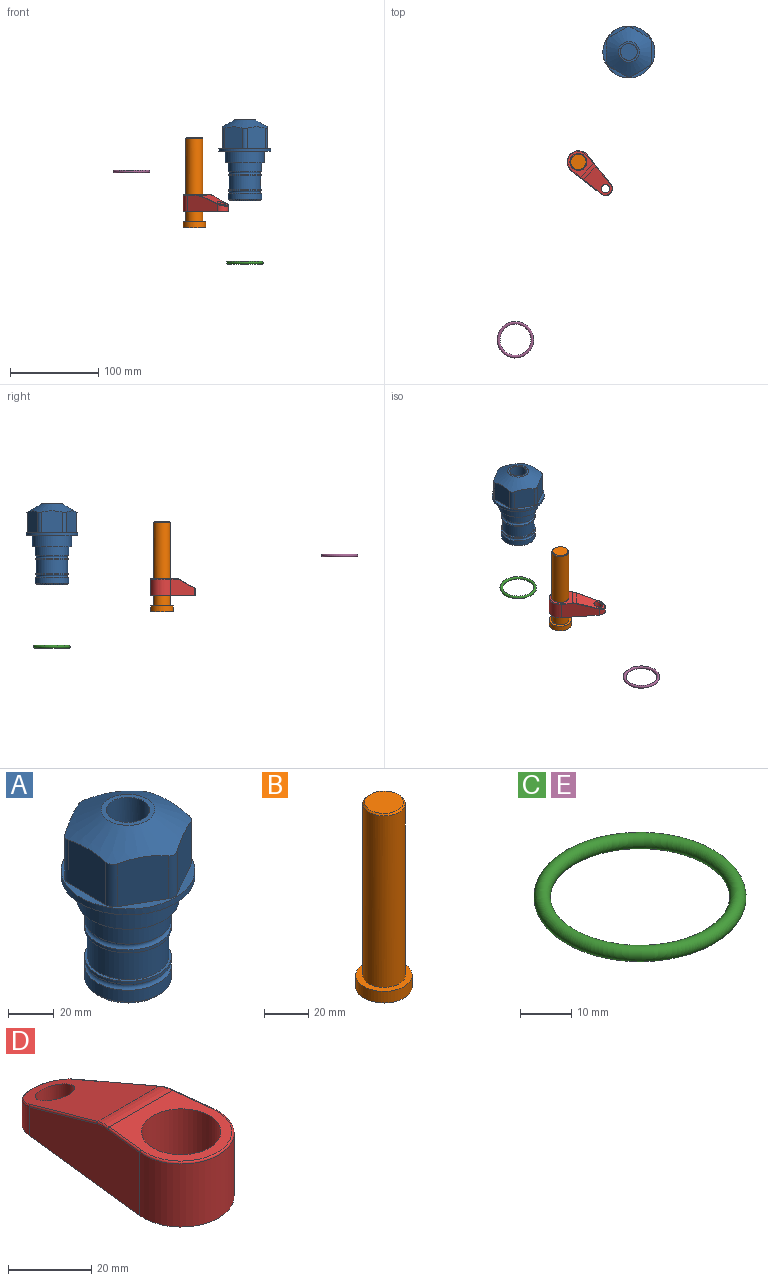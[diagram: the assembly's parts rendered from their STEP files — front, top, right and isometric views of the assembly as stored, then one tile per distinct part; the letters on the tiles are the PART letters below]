
ASSEMBLY  parts=5 mates=2
PART A: 36 faces, bbox 58.7x58.7x91.2 mm
  f0: cylinder r=17.78mm len=35.56mm, axis (0,0,1), area 1670.8mm2, adj f23,f24,f31
  f1: cylinder r=19.05mm len=38.1mm, axis (0,0,1), area 1191.9mm2, adj f26,f27,f30
  f2: plane 58.66x58.66mm, normal (0,0,-1), area 1150.6mm2, adj f3,f28
  f3: cylinder r=29.33mm len=58.66mm, axis (0,0,-1), area 585.1mm2, adj f2,f4
  f4: plane 58.66x58.66mm, normal (0,0,1), area 475.9mm2, adj f3,f5,f6,f7,f8,f9,f10,f11
  f5: plane 24.5x20.32mm, normal (-0.5,0.87,0), area 562.8mm2, adj f4,f15,f16,f17
  f6: plane 24.5x20.32mm, normal (0.5,0.87,0), area 562.8mm2, adj f4,f14,f15,f17
  f7: plane 24.5x23.48mm, normal (1,0,0), area 562.8mm2, adj f4,f13,f14,f17
  f8: plane 24.5x20.32mm, normal (0.5,-0.87,0), area 562.8mm2, adj f4,f12,f13,f17
  f9: plane 24.5x20.32mm, normal (-0.5,-0.87,0), area 562.8mm2, adj f4,f11,f12,f17
  f10: plane 24.5x23.48mm, normal (-1,0,0), area 562.8mm2, adj f4,f11,f16,f17
  f11: cylinder r=5.08mm len=23.01mm, axis (0,0,-1), area 121.2mm2, adj f4,f9,f10,f17
  f12: cylinder r=5.08mm len=23.01mm, axis (0,0,-1), area 121.2mm2, adj f4,f8,f9,f17
  f13: cylinder r=5.08mm len=23.01mm, axis (0,0,-1), area 121.2mm2, adj f4,f7,f8,f17
  f14: cylinder r=5.08mm len=23.01mm, axis (0,0,-1), area 121.2mm2, adj f4,f6,f7,f17
  f15: cylinder r=5.08mm len=23.01mm, axis (0,0,-1), area 121.2mm2, adj f4,f5,f6,f17
  f16: cylinder r=5.08mm len=23.01mm, axis (0,0,-1), area 121.2mm2, adj f4,f5,f10,f17
  f17: cone r=11.73mm half-angle=60deg, axis (0,0,-1), area 2071.8mm2, adj f5,f6,f7,f8,f9,f10,f11,f12
  f18: plane 23.46x23.46mm, normal (0,0,1), area 147.4mm2, adj f17,f35
  f19: plane 34.93x34.93mm, normal (0,0,-1), area 958mm2, adj f29
  f20: cylinder r=19.05mm len=38.1mm, axis (0,0,1), area 760.1mm2, adj f21,f29
  f21: torus R=19.05mm, axis (0,0,1), area 565.3mm2, adj f20,f22
  f22: cylinder r=19.05mm len=38.1mm, axis (0,0,1), area 190mm2, adj f21,f23
  f23: plane 38.1x38.1mm, normal (0,0,1), area 146.9mm2, adj f0,f22
  f24: plane 38.1x38.1mm, normal (0,0,-1), area 146.9mm2, adj f0,f25
  f25: cylinder r=19.05mm len=38.1mm, axis (0,0,1), area 190mm2, adj f24,f26
  f26: torus R=19.05mm, axis (0,0,1), area 565.3mm2, adj f1,f25
  f27: plane 44.45x44.45mm, normal (0,0,-1), area 411.7mm2, adj f1,f28
  f28: cylinder r=22.23mm len=44.45mm, axis (0,0,1), area 1773.5mm2, adj f2,f27
  f29: cone r=19.05mm half-angle=45deg, axis (0,0,1), area 257.5mm2, adj f19,f20
  f30: cylinder r=3.17mm len=6.75mm, axis (-1,0,0), area 128mm2, adj f1,f33
  f31: cylinder r=3.17mm len=6.35mm, axis (-1,0,0), area 102.5mm2, adj f0,f33
  f32: plane 25.4x25.4mm, normal (0,0,1), area 506.7mm2, adj f33
  f33: cylinder r=12.7mm len=66.42mm, axis (0,0,-1), area 5236.2mm2, adj f30,f31,f32,f34
  f34: cone r=9.53mm half-angle=30deg, axis (0,0,-1), area 443.4mm2, adj f33,f35
  f35: cylinder r=9.53mm len=19.05mm, axis (0,0,-1), area 849mm2, adj f18,f34
PART B: 6 faces, bbox 25.4x25.4x101.6 mm
  f0: plane 17.46x17.46mm, normal (0,0,1), area 239.5mm2, adj f5
  f1: plane 25.4x25.4mm, normal (0,0,-1), area 506.7mm2, adj f2
  f2: cylinder r=12.7mm len=25.4mm, axis (0,0,1), area 506.7mm2, adj f1,f3
  f3: plane 25.4x25.4mm, normal (0,0,1), area 221.7mm2, adj f2,f4
  f4: cylinder r=9.53mm len=94.46mm, axis (0,0,1), area 5653mm2, adj f3,f5
  f5: cone r=8.73mm half-angle=45deg, axis (0,0,-1), area 64.4mm2, adj f0,f4
PART C: 1 faces, bbox 44.7x44.7x3.2 mm
  f0: torus R=19.05mm, axis (0,0,1), area 1193.9mm2
PART D: 44 faces, bbox 27.5x64.5x19.1 mm
  f0: plane 2.3x0.95mm, normal (0,0,-1), area 1mm2, adj f25,f30,f34
  f1: plane 63.5x25.4mm, normal (0,0,-1), area 561.7mm2, adj f2,f3,f4,f5,f6,f7,f19,f20
  f2: cylinder r=12.7mm len=25.4mm, axis (0,0,-1), area 792.2mm2, adj f1,f3,f5,f13
  f3: plane 42.33x18.54mm, normal (0.99,0.11,0), area 647mm2, adj f1,f2,f4,f11,f12,f14
  f4: cylinder r=7.94mm len=15.78mm, axis (0,0,-1), area 158.6mm2, adj f1,f3,f5,f16
  f5: plane 42.33x18.54mm, normal (-0.99,0.11,0), area 647mm2, adj f1,f2,f4,f15,f17,f18
  f6: cylinder r=9.53mm len=19.05mm, axis (0,0,-1), area 1140.1mm2, adj f1,f8
  f7: cylinder r=4.76mm len=10.98mm, axis (0,0,-1), area 276.1mm2, adj f1,f9
  f8: plane 25.83x24.38mm, normal (0,0,1), area 262.2mm2, adj f6,f10,f11,f13,f15
  f9: plane 32.49x20.55mm, normal (0,0.34,0.94), area 489.9mm2, adj f7,f10,f14,f16,f18
  f10: cylinder r=12.7mm len=21.49mm, axis (-1,0,0), area 93.2mm2, adj f8,f9,f12,f17
  f11: cylinder r=0.51mm len=12.34mm, axis (0.11,-0.99,0), area 9.9mm2, adj f3,f8,f12,f13
  f12: bspline ~7.62x1.64mm, area 3.5mm2, adj f3,f10,f11,f14
  f13: torus R=12.19mm, axis (0,0,1), area 33.6mm2, adj f2,f8,f11,f15
  f14: cylinder r=0.51mm len=26.01mm, axis (0.1,-0.93,0.34), area 21.6mm2, adj f3,f9,f12,f16
  f15: cylinder r=0.51mm len=12.34mm, axis (0.11,0.99,0), area 9.9mm2, adj f5,f8,f13,f17
  f16: bspline ~15.78x7.05mm, area 15.7mm2, adj f4,f9,f14,f18
  f17: bspline ~7.62x1.64mm, area 3.5mm2, adj f5,f10,f15,f18
  f18: cylinder r=0.51mm len=26.01mm, axis (0.1,0.93,-0.34), area 21.6mm2, adj f5,f9,f16,f17
  f19: plane 21.6x14.29mm, normal (-0.99,-0.11,0), area 242.6mm2, adj f1,f26,f28,f34,f36,f38
  f20: plane 21.6x14.29mm, normal (0.99,-0.11,0), area 242.6mm2, adj f1,f27,f29,f37,f39,f41
  f21: cylinder r=12.7mm len=14.29mm, axis (0,0,-1), area 173.2mm2, adj f1,f26,f27,f30,f31,f33
  f22: cylinder r=7.94mm len=7.63mm, axis (0,0,-1), area 53.8mm2, adj f1,f28,f29,f42
  f23: plane 2.3x0.95mm, normal (0,0,-1), area 1mm2, adj f25,f33,f37
  f24: plane 17.94x12.32mm, normal (0,-0.34,-0.94), area 191.2mm2, adj f25,f38,f41,f42
  f25: cylinder r=9.53mm len=12.93mm, axis (-1,0,0), area 37.5mm2, adj f0,f23,f24,f31,f36,f39
  f26: cylinder r=1.59mm len=14.29mm, axis (0,0,-1), area 49mm2, adj f1,f19,f21,f32
  f27: cylinder r=1.59mm len=14.29mm, axis (0,0,-1), area 49mm2, adj f1,f20,f21,f35
  f28: cylinder r=1.59mm len=7.28mm, axis (0,0,-1), area 22.1mm2, adj f1,f19,f22,f40
  f29: cylinder r=1.59mm len=7.28mm, axis (0,0,-1), area 22.1mm2, adj f1,f20,f22,f43
  f30: torus R=14.29mm, axis (0,0,1), area 5.8mm2, adj f0,f21,f31,f32
  f31: bspline ~11.06x2.73mm, area 20.8mm2, adj f21,f25,f30,f33
  f32: sphere r=1.59mm, area 5.4mm2, adj f26,f30,f34
  f33: torus R=14.29mm, axis (0,0,1), area 5.8mm2, adj f21,f23,f31,f35
  f34: cylinder r=1.59mm len=1.68mm, axis (-0.11,0.99,0), area 2.4mm2, adj f0,f19,f32,f36
  f35: sphere r=1.59mm, area 5.4mm2, adj f27,f33,f37
  f36: bspline ~5.82x2.33mm, area 7.7mm2, adj f19,f25,f34,f38
  f37: cylinder r=1.59mm len=1.68mm, axis (0.11,0.99,0), area 2.4mm2, adj f20,f23,f35,f39
  f38: cylinder r=1.59mm len=18.33mm, axis (0.1,-0.93,0.34), area 46.7mm2, adj f19,f24,f36,f40
  f39: bspline ~5.82x2.33mm, area 7.7mm2, adj f20,f25,f37,f41
  f40: sphere r=1.59mm, area 3.6mm2, adj f28,f38,f42
  f41: cylinder r=1.59mm len=18.33mm, axis (0.1,0.93,-0.34), area 46.7mm2, adj f20,f24,f39,f43
  f42: bspline ~8.31x1.84mm, area 15.3mm2, adj f22,f24,f40,f43
  f43: sphere r=1.59mm, area 3.6mm2, adj f29,f41,f42
PART E: same geometry as C
PLACE A t=(128.27,325.41,-1.63)mm
PLACE B t=(71.22,201.06,-59.88)mm fixed
PLACE C t=(128.27,325.41,-103.07)mm
PLACE D rot(axis=(0,0,-1),134.5deg) t=(71.22,201.06,-69.58)mm
PLACE E at identity
MATE cylindrical C.f0 <-> A.f0  axis (0,0,1) through (128.27,325.41,-127.58)mm
MATE cylindrical D.f2 <-> B.f2  axis (0,0,-1) through (71.22,201.06,-50.53)mm
